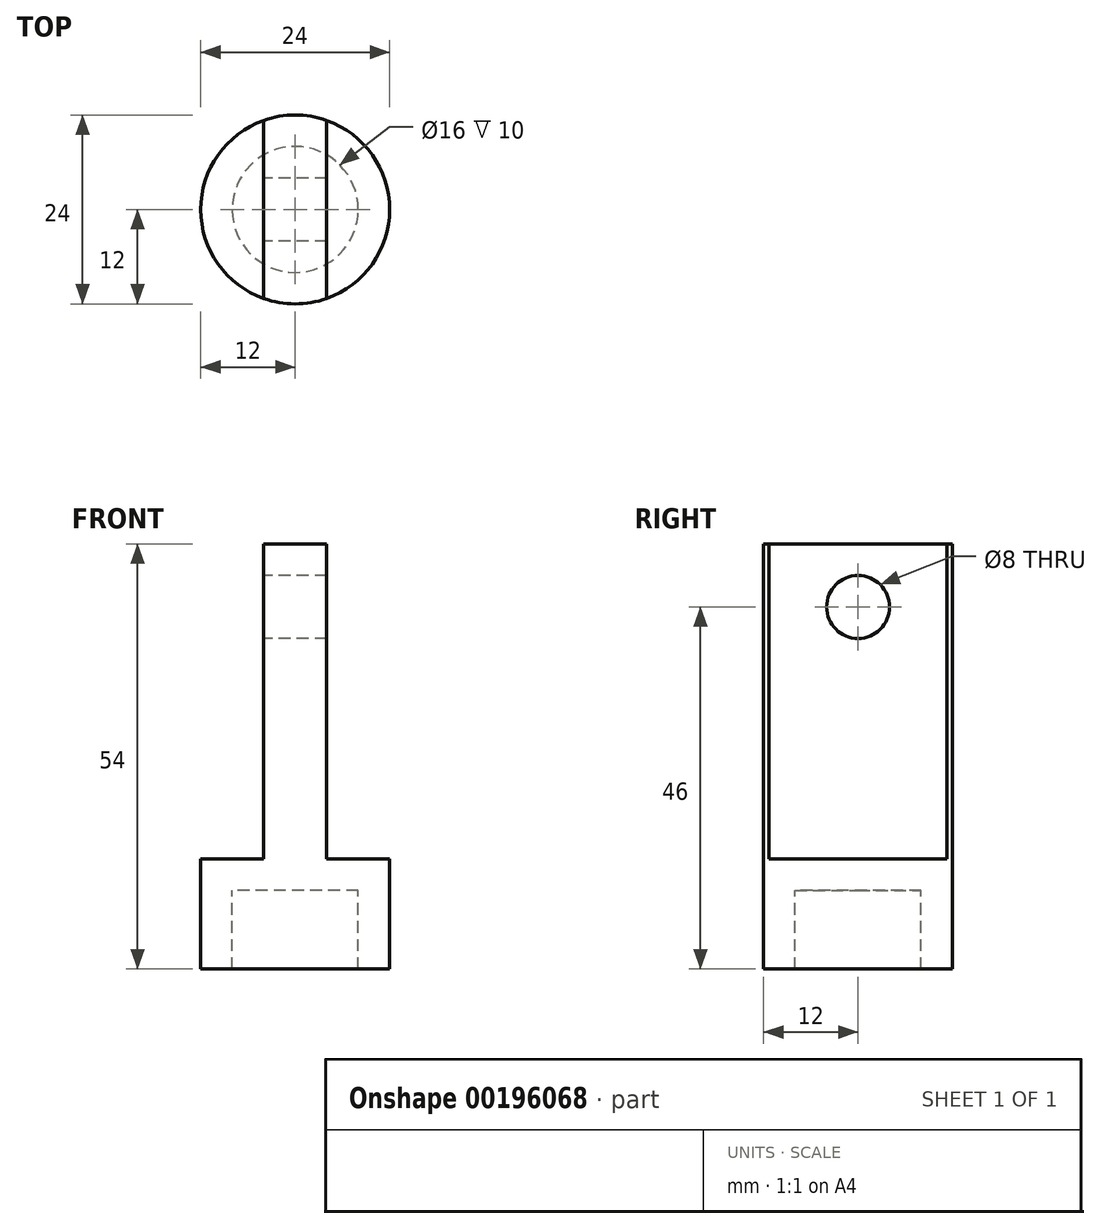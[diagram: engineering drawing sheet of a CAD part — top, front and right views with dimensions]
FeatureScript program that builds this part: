
annotation { "Feature Type Name" : "Feature", "Feature Type Description" : "" }
export const myFeature = defineFeature(function(context is Context, id is Id, definition is map)
    precondition{}
    {
        {
            var Q0;
            Q0=qCreatedBy(makeId("Top.planeOp"),FACE);
            var sketch = newSketch(context, id + "F0", { "sketchPlane" : qUnion([Q0])});
            skCircle(sketch, "E0", {"center": v(0, 0) * mm, "radius": 12 * mm});
            skSolve(sketch);
        }
        {
            var Q0;
            Q0 = qSketchRegion(id + "F0", true);
            extrude(context, id + "F1", {"entities" : qUnion([Q0]), "depth" : 10 * mm});
        }
        {
            var Q0;
            Q0=makeQuery(id+"F1.opExtrude","CAP_FACE",FACE,{"disambiguationData":[OSD([sQuery(id+"F0.wireOp",EDGE,"E0")])],"isStart":false});
            var sketch = newSketch(context, id + "F2", { "sketchPlane" : qUnion([Q0])});
            skPoint(sketch, "E1.center.orphan", {"position": v(0, 0) * mm});
            skCircle(sketch, "E2", {"center": v(0, 0) * mm, "radius": 8 * mm});
            skSolve(sketch);
        }
        {
            var Q0;
            Q0 = qSketchRegion(id + "F2", true);
            extrude(context, id + "F3", {"entities" : qUnion([Q0]), "operationType" : NewBodyOperationType.REMOVE, "oppositeDirection" : true, "depth" : 25 * mm});
        }
        {
            var Q0;
            Q0=makeQuery(id+"F1.opExtrude","CAP_FACE",FACE,{"disambiguationData":[OSD([sQuery(id+"F0.wireOp",EDGE,"E0")])],"isStart":false});
            var sketch = newSketch(context, id + "F4", { "sketchPlane" : qUnion([Q0])});
            skCircle(sketch, "E3.0", {"center": v(0, 0) * mm, "radius": 12 * mm});
            skSolve(sketch);
        }
        {
            var Q0;
            Q0 = qSketchRegion(id + "F4", true);
            extrude(context, id + "F5", {"entities" : qUnion([Q0]), "operationType" : NewBodyOperationType.ADD, "depth" : 4 * mm});
        }
        {
            var Q0;
            Q0=makeQuery(id+"F5.opExtrude","CAP_FACE",FACE,{"disambiguationData":[OSD([sQuery(id+"F4.wireOp",EDGE,"E3.0")])],"isStart":false});
            var sketch = newSketch(context, id + "F6", { "sketchPlane" : qUnion([Q0])});
            skArc(sketch, "E4.0", {"start": v(4, 11.31) * mm, "mid": v(0, 12) * mm, "end": v(-4, 11.31) * mm});
            skLineSegment(sketch, "E5.left", {"start": v(-4, 11.31) * mm, "end": v(-4, -11.31) * mm});
            skLineSegment(sketch, "E5.right", {"start": v(4, 11.31) * mm, "end": v(4, -11.31) * mm});
            skArc(sketch, "E6.trimOffspring", {"start": v(-4, -11.31) * mm, "mid": v(0, -12) * mm, "end": v(4, -11.31) * mm});
            skSolve(sketch);
        }
        {
            var Q0;
            Q0 = qSketchRegion(id + "F6", true);
            extrude(context, id + "F7", {"entities" : qUnion([Q0]), "operationType" : NewBodyOperationType.ADD, "depth" : 40 * mm});
        }
        {
            var Q0;
            Q0=makeQuery(id+"F7.opExtrude","SWEPT_FACE",FACE,{"disambiguationData":[OSD([sQuery(id+"F6.wireOp",EDGE,"E5.left")])]});
            var sketch = newSketch(context, id + "F8", { "sketchPlane" : qUnion([Q0])});
            skCircle(sketch, "E7", {"center": v(0, 46) * mm, "radius": 4 * mm});
            skSolve(sketch);
        }
        {
            var Q0;
            Q0 = qSketchRegion(id + "F8", true);
            extrude(context, id + "F9", {"entities" : qUnion([Q0]), "operationType" : NewBodyOperationType.REMOVE, "oppositeDirection" : true, "depth" : 25 * mm});
        }
    });
